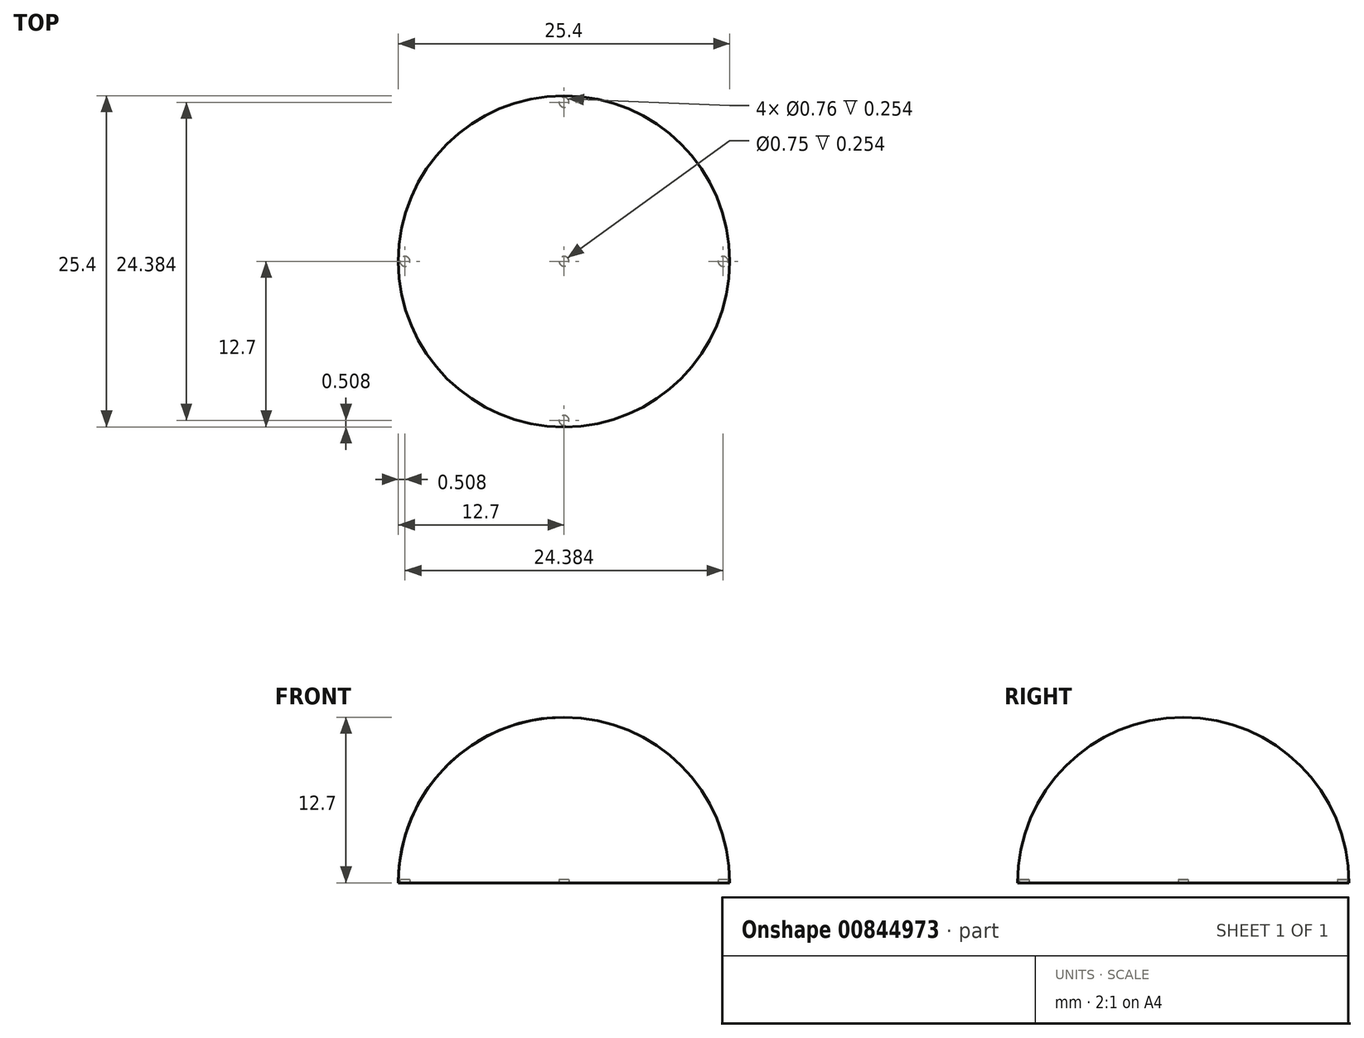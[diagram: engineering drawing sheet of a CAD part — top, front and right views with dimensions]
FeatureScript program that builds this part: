
annotation { "Feature Type Name" : "Feature", "Feature Type Description" : "" }
export const myFeature = defineFeature(function(context is Context, id is Id, definition is map)
    precondition{}
    {
        {
            var Q0;
            Q0=qCreatedBy(makeId("Front.planeOp"),FACE);
            var sketch = newSketch(context, id + "F0", { "sketchPlane" : qUnion([Q0])});
            skArc(sketch, "E0", {"start": v(0, -12.7) * mm, "mid": v(12.7, 0) * mm, "end": v(0, 12.7) * mm});
            skLineSegment(sketch, "E1", {"start": v(0, 12.7) * mm, "end": v(0, -12.7) * mm});
            skSolve(sketch);
        }
        {
            var Q0;
            Q0=makeQuery(id+"F0.imprint","IMPRINT",FACE,{"disambiguationData":[TD([[makeQuery(id+"F0.imprint","IMPRINT",EDGE,{"derivedFrom":sQuery(id+"F0.wireOp",EDGE,"E0")}),1.0]])]});
            var Q1;
            Q1=sQuery(id+"F0.wireOp",EDGE,"E1");
            revolve(context, id + "F1", {"surfaceOperationType" : NewSurfaceOperationType.NEW, "entities" : qUnion([Q0]), "axis" : qUnion([Q1]), "revolveType" : RevolveType.FULL});
        }
        {
            var Q0;
            Q0=qCreatedBy(makeId("Top.planeOp"),FACE);
            cPlane(context, id + "F2", {"entities" : qUnion([Q0]), "cplaneType" : CPlaneType.OFFSET, "offset" : 0 * mm, "width" : 152.4 * mm, "height" : 152.4 * mm});
        }
        {
            var Q0;
            Q0=qCreatedBy(id+"F2.planeOp",FACE);
            var sketch = newSketch(context, id + "F3", { "sketchPlane" : qUnion([Q0])});
            skLineSegment(sketch, "E2.bottom", {"start": v(14.85, -12.85) * mm, "end": v(-14.85, -12.85) * mm});
            skLineSegment(sketch, "E2.top", {"start": v(14.85, 12.85) * mm, "end": v(-14.85, 12.85) * mm});
            skLineSegment(sketch, "E2.left", {"start": v(14.85, -12.85) * mm, "end": v(14.85, 12.85) * mm});
            skLineSegment(sketch, "E2.right", {"start": v(-14.85, -12.85) * mm, "end": v(-14.85, 12.85) * mm});
            skPoint(sketch, "E2.middle", {"position": v(0, 0) * mm});
            skSolve(sketch);
        }
        {
            var Q0;
            Q0 = qSketchRegion(id + "F3", true);
            extrude(context, id + "F4", {"entities" : qUnion([Q0]), "operationType" : NewBodyOperationType.REMOVE, "oppositeDirection" : true, "depth" : 25.4 * mm, "offsetDistance" : 25.4 * mm});
        }
        {
            var Q0;
            Q0=qCreatedBy(makeId("Top.planeOp"),FACE);
            var sketch = newSketch(context, id + "F5", { "sketchPlane" : qUnion([Q0])});
            skCircle(sketch, "E3", {"center": v(0, 0) * mm, "radius": 0.38 * mm});
            skCircle(sketch, "E4", {"center": v(0, -12.2) * mm, "radius": 0.38 * mm});
            skCircle(sketch, "E5", {"center": v(0, 12.2) * mm, "radius": 0.38 * mm});
            skCircle(sketch, "E6", {"center": v(12.2, 0) * mm, "radius": 0.38 * mm});
            skCircle(sketch, "E7", {"center": v(-12.2, 0) * mm, "radius": 0.38 * mm});
            skSolve(sketch);
        }
        {
            var Q0;
            Q0=makeQuery(id+"F5.imprint","IMPRINT",FACE,{"disambiguationData":[TD([[makeQuery(id+"F5.imprint","IMPRINT",EDGE,{"derivedFrom":sQuery(id+"F5.wireOp",EDGE,"E3")}),1.0]])]});
            extrude(context, id + "F6", {"entities" : qUnion([Q0]), "operationType" : NewBodyOperationType.REMOVE, "depth" : 0.25 * mm, "offsetDistance" : 25.4 * mm});
        }
        {
            var Q0;
            Q0 = qSketchRegion(id + "F5", true);
            extrude(context, id + "F7", {"entities" : qUnion([Q0]), "operationType" : NewBodyOperationType.REMOVE, "depth" : 0.25 * mm, "offsetDistance" : 25.4 * mm});
        }
    });
